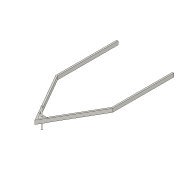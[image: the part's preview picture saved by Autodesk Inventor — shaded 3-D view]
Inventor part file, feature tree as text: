
AUTODESK INVENTOR PART (.ipt)
format: ipt  version: 2018 (Build 220112000, 112)  size: 121,856 bytes
history: native  units: in
note: dims shown in document units (in); Inventor stores cm internally (conversion verified against a paired STEP export)
features: extrude x5, sketch x5
ambient origin geometry x8: Origin, YZ Plane, XZ Plane, XY Plane, X Axis, Y Axis, Z Axis, Center Point
bodies: Solid1 (feature_tree)
feature tree (10):
  extrude  "Extrusion1"  Depth=2.0in
  extrude  "Extrusion2"  Depth=24.5in
  extrude  "Extrusion3"  Depth=5.0in TaperAngle=0.0deg
  extrude  "Extrusion4"  Depth=0.25in TaperAngle=0.0deg
  extrude  "Extrusion5"  Depth=2.0in
  sketch  "Sketch1"  dims[d0=82.0in d1=2.0in]
  sketch  "Sketch2"  dims[d3=150.0deg d4=24.5in]
  sketch  "Sketch3"  dims[d5=2.0in d6=5.0in d7=0.0in]
  sketch  "Sketch4"  dims[d8=12.0in d9=0.25in d10=0.0in]
  sketch  "Sketch5"  dims[d11=0.25in d12=0.0in d13=2.0in d14=2.0in d15=12.0in d16=0.0in d17=2.0in d18=2.0in d19=10.75in d20=0.0in d21=87.5in]
